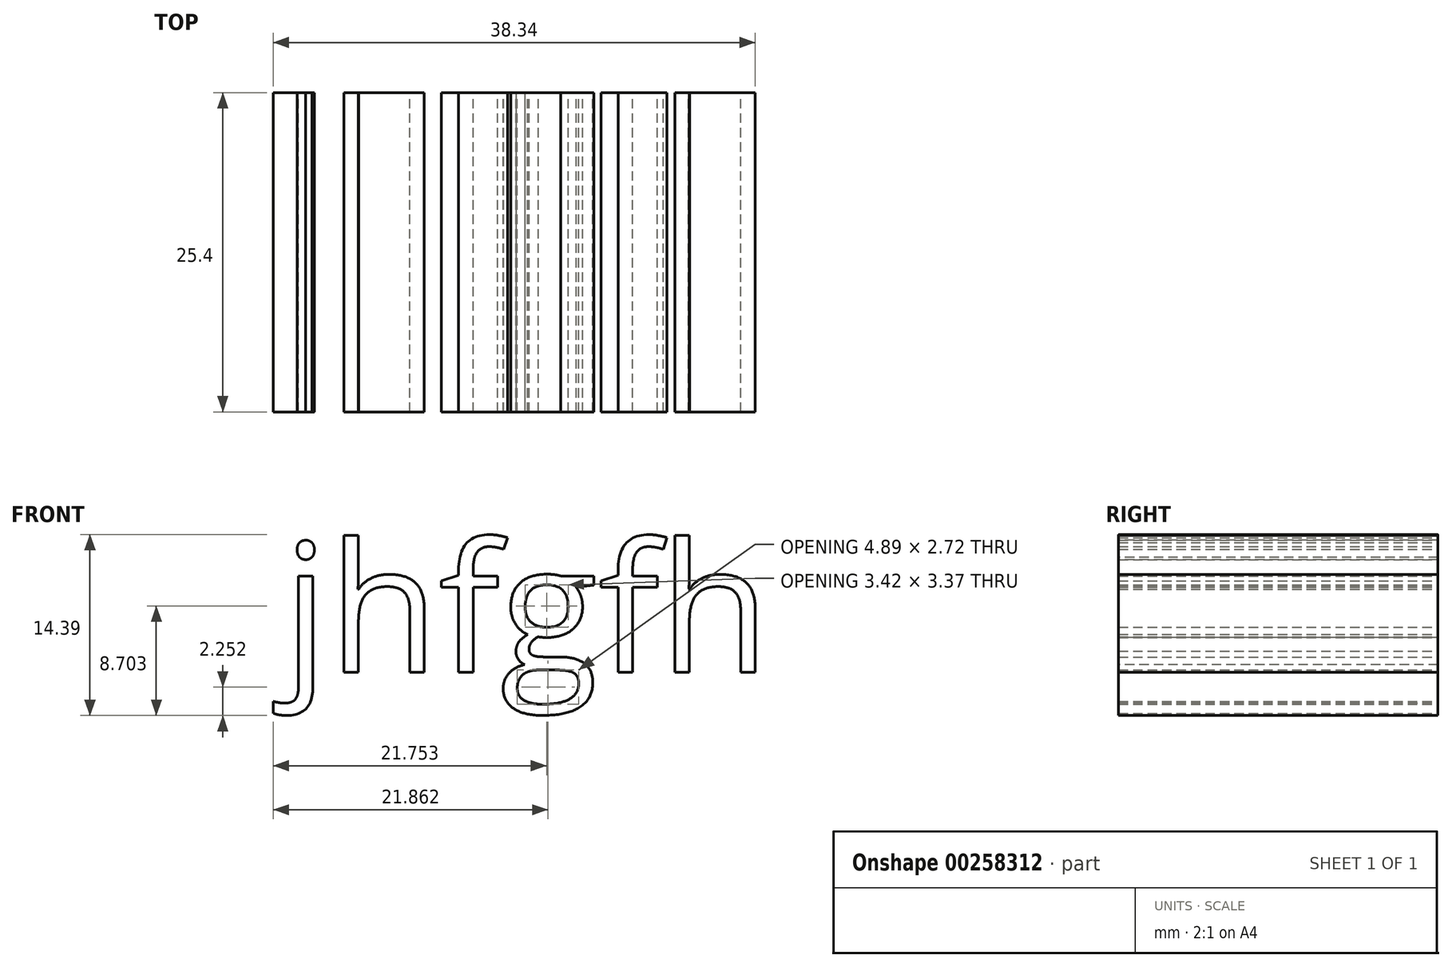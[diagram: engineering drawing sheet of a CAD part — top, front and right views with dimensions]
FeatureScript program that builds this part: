
annotation { "Feature Type Name" : "Feature", "Feature Type Description" : "" }
export const myFeature = defineFeature(function(context is Context, id is Id, definition is map)
    precondition{}
    {
        {
            var Q0;
            Q0=qCreatedBy(makeId("Front.planeOp"),FACE);
            var sketch = newSketch(context, id + "F0", { "sketchPlane" : qUnion([Q0])});
            skText(sketch, "E0", { "text": "jhfgfh", "fontName": "OpenSans-Regular.ttf"});
            const initialGuessF0  = {"E0": [-0.06654, 0.054, 1, 0, 0.0103]};
            skSetInitialGuess(sketch, initialGuessF0);
            skSolve(sketch);
        }
        {
            var Q0;
            Q0 = qSketchRegion(id + "F0", true);
            extrude(context, id + "F1", {"entities" : qUnion([Q0]), "depth" : 25.4 * mm});
        }
    });
